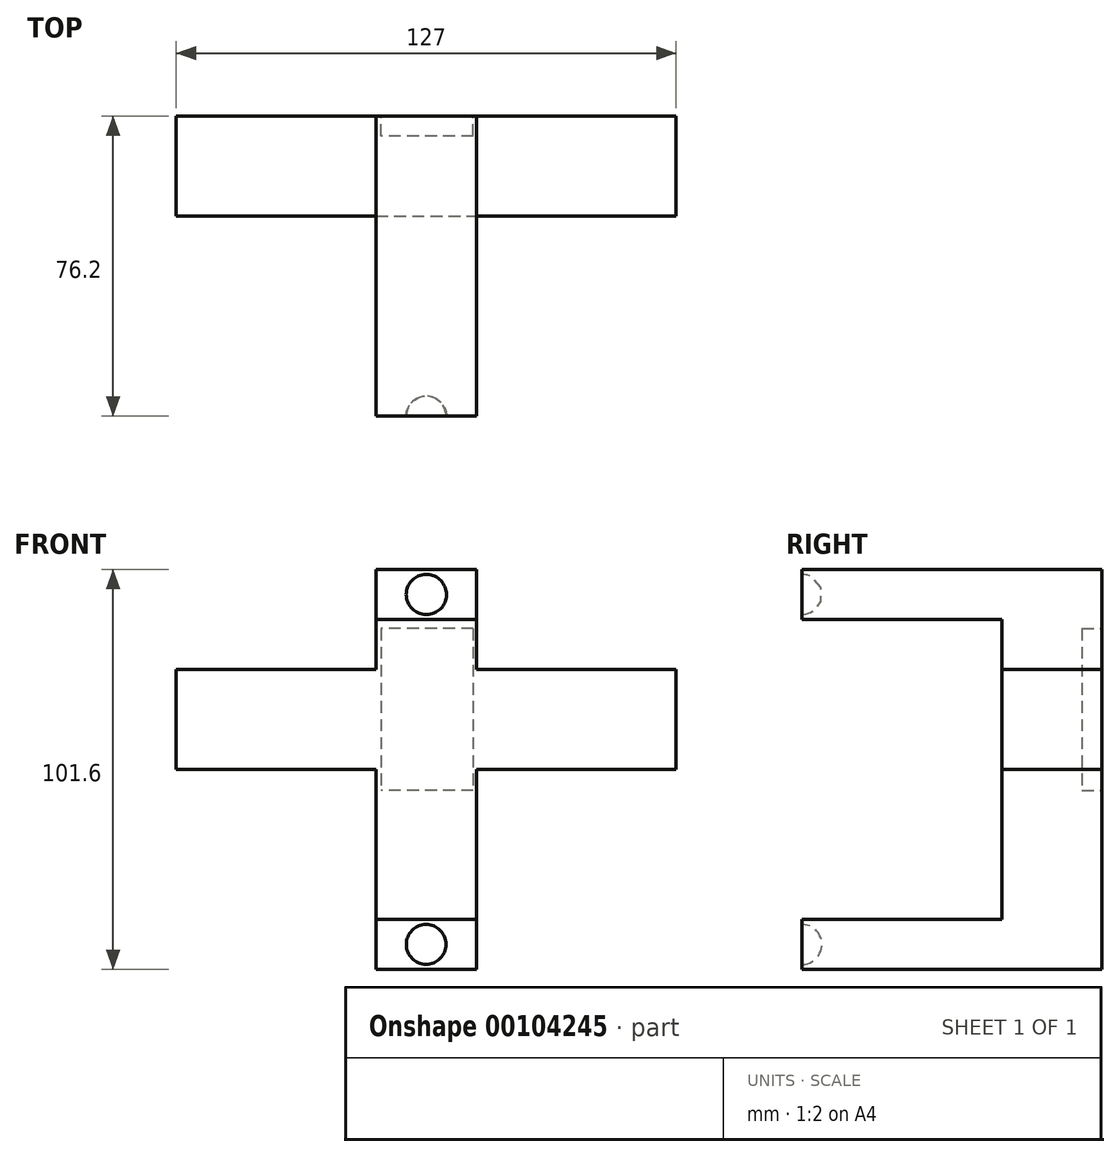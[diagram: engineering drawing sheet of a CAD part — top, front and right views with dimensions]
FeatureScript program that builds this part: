
annotation { "Feature Type Name" : "Feature", "Feature Type Description" : "" }
export const myFeature = defineFeature(function(context is Context, id is Id, definition is map)
    precondition{}
    {
        {
            var Q0;
            Q0=qCreatedBy(makeId("Front.planeOp"),FACE);
            var sketch = newSketch(context, id + "F0", { "sketchPlane" : qUnion([Q0])});
            skLineSegment(sketch, "E0.bottom", {"start": v(-67.58, 4.59) * mm, "end": v(59.42, 4.59) * mm});
            skLineSegment(sketch, "E0.top", {"start": v(-67.58, -20.81) * mm, "end": v(59.42, -20.81) * mm});
            skLineSegment(sketch, "E0.left", {"start": v(-67.58, 4.59) * mm, "end": v(-67.58, -20.81) * mm});
            skLineSegment(sketch, "E0.right", {"start": v(59.42, 4.59) * mm, "end": v(59.42, -20.81) * mm});
            skSolve(sketch);
        }
        {
            var Q0;
            Q0=makeQuery(id+"F0.imprint","IMPRINT",FACE,{"disambiguationData":[TD([[makeQuery(id+"F0.imprint","IMPRINT",EDGE,{"derivedFrom":sQuery(id+"F0.wireOp",EDGE,"E0.bottom")}),-1.0]])]});
            extrude(context, id + "F1", {"entities" : qUnion([Q0]), "depth" : 25.4 * mm});
        }
        {
            var Q0;
            Q0=makeQuery(id+"F1.opExtrude","SWEPT_FACE",FACE,{"disambiguationData":[OSD([sQuery(id+"F0.wireOp",EDGE,"E0.top")])]});
            var sketch = newSketch(context, id + "F2", { "sketchPlane" : qUnion([Q0])});
            skLineSegment(sketch, "E1", {"start": v(-16.78, 25.4) * mm, "end": v(-16.78, 0) * mm});
            skLineSegment(sketch, "E2", {"start": v(8.69, 25.4) * mm, "end": v(8.69, 0) * mm});
            skSolve(sketch);
        }
        {
            var Q0;
            {var subQ0=sQuery(id+"F2.wireOp",EDGE,"E1");Q0=makeQuery(id+"F2.imprint","IMPRINT",FACE,{"disambiguationData":[TD([[makeQuery(id+"F2.imprint","IMPRINT",EDGE,{"derivedFrom":subQ0}),1.0]])]});}
            extrude(context, id + "F3", {"entities" : qUnion([Q0]), "operationType" : NewBodyOperationType.ADD, "endBound" : BoundingType.SYMMETRIC, "depth" : 101.6 * mm});
        }
        {
            var Q0;
            {var subQ0=sQuery(id+"F0.wireOp",EDGE,"E0.top");var subQ1=makeQuery(id+"F1.opExtrude","CAP_EDGE",EDGE,{"disambiguationData":[OSD([subQ0])],"isStart":false});Q0=makeQuery(id+"F3.boolean.opBoolean","MERGE",FACE,{"derivedFrom":[makeQuery(id+"F1.opExtrude","CAP_FACE",FACE,{"disambiguationData":[OSD([sQuery(id+"F0.wireOp",EDGE,"E0.bottom"),subQ0,sQuery(id+"F0.wireOp",EDGE,"E0.left"),sQuery(id+"F0.wireOp",EDGE,"E0.right")])],"isStart":false}),makeQuery(id+"F3.opExtrude","SWEPT_FACE",FACE,{"disambiguationData":[OSD([subQ0]),TDD([makeQuery(id+"F2.imprint","IMPRINT",EDGE,{"disambiguationData":[TD([[makeQuery(id+"F2.imprint","INTERSECT",VERTEX,{"derivedFrom":[subQ1,sQuery(id+"F2.wireOp",EDGE,"E1")]}),-1.0]])],"derivedFrom":subQ1})])]})]});}
            var sketch = newSketch(context, id + "F4", { "sketchPlane" : qUnion([Q0])});
            skLineSegment(sketch, "E3", {"start": v(-16.78, 17.29) * mm, "end": v(8.69, 17.29) * mm});
            skLineSegment(sketch, "E4", {"start": v(-16.78, -58.91) * mm, "end": v(8.69, -58.91) * mm});
            skSolve(sketch);
        }
        {
            var Q0;
            {var subQ0=sQuery(id+"F4.wireOp",EDGE,"E3");Q0=makeQuery(id+"F4.imprint","IMPRINT",FACE,{"disambiguationData":[TD([[makeQuery(id+"F4.imprint","IMPRINT",EDGE,{"derivedFrom":subQ0}),1.0]])]});}
            var Q1;
            {var subQ0=sQuery(id+"F4.wireOp",EDGE,"E4");Q1=makeQuery(id+"F4.imprint","IMPRINT",FACE,{"disambiguationData":[TD([[makeQuery(id+"F4.imprint","IMPRINT",EDGE,{"derivedFrom":subQ0}),-1.0]])]});}
            extrude(context, id + "F5", {"entities" : qUnion([Q0, Q1]), "operationType" : NewBodyOperationType.ADD, "depth" : 50.8 * mm});
        }
        {
            var Q0;
            Q0=makeQuery(id+"F5.opExtrude","CAP_FACE",FACE,{"disambiguationData":[OSD([sQuery(id+"F0.wireOp",EDGE,"E0.top"),sQuery(id+"F2.wireOp",EDGE,"E1"),sQuery(id+"F2.wireOp",EDGE,"E2"),sQuery(id+"F4.wireOp",EDGE,"E3")])],"isStart":false});
            var sketch = newSketch(context, id + "F6", { "sketchPlane" : qUnion([Q0])});
            skLineSegment(sketch, "E5", {"start": v(-16.78, 28.72) * mm, "end": v(8.69, 28.72) * mm});
            skLineSegment(sketch, "E6", {"start": v(8.69, 28.72) * mm, "end": v(8.69, 29.99) * mm});
            skLineSegment(sketch, "E7", {"start": v(-16.78, 18.56) * mm, "end": v(8.69, 18.56) * mm});
            skLineSegment(sketch, "E8", {"start": v(8.69, 18.56) * mm, "end": v(8.69, 17.29) * mm});
            skLineSegment(sketch, "E9", {"start": v(-4.05, 18.56) * mm, "end": v(-4, 28.72) * mm});
            skLineSegment(sketch, "E10", {"start": v(-9.16, 28.72) * mm, "end": v(-9.16, 18.56) * mm});
            skArc(sketch, "E11", {"start": v(-4, 28.72) * mm, "mid": v(-9.14, 23.66) * mm, "end": v(-4.05, 18.56) * mm});
            skSolve(sketch);
        }
        {
            var Q0;
            {var subQ1=sQuery(id+"F6.wireOp",EDGE,"E9");Q0=makeQuery(id+"F6.imprint","IMPRINT",FACE,{"disambiguationData":[TD([[makeQuery(id+"F6.imprint","IMPRINT",EDGE,{"derivedFrom":subQ1}),1.0]])]});}
            var Q1;
            Q1=sQuery(id+"F6.wireOp",EDGE,"E9");
            revolve(context, id + "F7", {"operationType" : NewBodyOperationType.REMOVE, "entities" : qUnion([Q0]), "axis" : qUnion([Q1]), "revolveType" : RevolveType.FULL, "oppositeDirection" : true});
        }
        {
            var Q0;
            Q0=makeQuery(id+"F5.opExtrude","CAP_FACE",FACE,{"disambiguationData":[OSD([sQuery(id+"F0.wireOp",EDGE,"E0.top"),sQuery(id+"F2.wireOp",EDGE,"E1"),sQuery(id+"F2.wireOp",EDGE,"E2"),sQuery(id+"F4.wireOp",EDGE,"E4")])],"isStart":false});
            var sketch = newSketch(context, id + "F8", { "sketchPlane" : qUnion([Q0])});
            skLineSegment(sketch, "E12", {"start": v(8.69, -60.18) * mm, "end": v(8.69, -58.91) * mm});
            skLineSegment(sketch, "E13", {"start": v(-4.08, -60.18) * mm, "end": v(-4.08, -70.34) * mm});
            skPoint(sketch, "E13.startSnap0", {"position": v(-4.05, -60.18) * mm});
            skLineSegment(sketch, "E14", {"start": v(-9.16, -60.18) * mm, "end": v(-9.16, -70.34) * mm});
            skArc(sketch, "E15", {"start": v(-4.05, -60.18) * mm, "mid": v(-9.13, -65.24) * mm, "end": v(-4.08, -70.34) * mm});
            skSolve(sketch);
        }
        {
            var Q0;
            {var subQ0=sQuery(id+"F8.wireOp",EDGE,"E15");var subQ1=sQuery(id+"F8.wireOp",EDGE,"E13");var subQ2=makeQuery(id+"F8.imprint","INTERSECT",VERTEX,{"disambiguationData":[OD(0.0)],"derivedFrom":[subQ1,subQ0]});Q0=makeQuery(id+"F8.imprint","IMPRINT",FACE,{"disambiguationData":[TD([[makeQuery(id+"F8.imprint","IMPRINT",EDGE,{"disambiguationData":[TD([[subQ2,1.0]])],"derivedFrom":subQ1}),-1.0]])]});}
            var Q1;
            Q1=sQuery(id+"F8.wireOp",EDGE,"E13");
            revolve(context, id + "F9", {"operationType" : NewBodyOperationType.REMOVE, "entities" : qUnion([Q0]), "axis" : qUnion([Q1]), "revolveType" : RevolveType.FULL, "oppositeDirection" : true});
        }
        {
            var Q0;
            {var subQ0=sQuery(id+"F0.wireOp",EDGE,"E0.top");var subQ1=makeQuery(id+"F1.opExtrude","CAP_EDGE",EDGE,{"disambiguationData":[OSD([subQ0])],"isStart":true});Q0=makeQuery(id+"F3.boolean.opBoolean","MERGE",FACE,{"derivedFrom":[makeQuery(id+"F1.opExtrude","CAP_FACE",FACE,{"disambiguationData":[OSD([sQuery(id+"F0.wireOp",EDGE,"E0.bottom"),subQ0,sQuery(id+"F0.wireOp",EDGE,"E0.left"),sQuery(id+"F0.wireOp",EDGE,"E0.right")])],"isStart":true}),makeQuery(id+"F3.opExtrude","SWEPT_FACE",FACE,{"disambiguationData":[OSD([subQ0]),TDD([makeQuery(id+"F2.imprint","IMPRINT",EDGE,{"disambiguationData":[TD([[makeQuery(id+"F2.imprint","INTERSECT",VERTEX,{"derivedFrom":[subQ1,sQuery(id+"F2.wireOp",EDGE,"E1")]}),-1.0]])],"derivedFrom":subQ1})])]})]});}
            var sketch = newSketch(context, id + "F10", { "sketchPlane" : qUnion([Q0])});
            skLineSegment(sketch, "E16.bottom", {"start": v(-7.85, 14.96) * mm, "end": v(15.51, 14.96) * mm});
            skLineSegment(sketch, "E16.top", {"start": v(-7.85, -26.19) * mm, "end": v(15.51, -26.19) * mm});
            skLineSegment(sketch, "E16.left", {"start": v(-7.85, 14.96) * mm, "end": v(-7.85, -26.19) * mm});
            skLineSegment(sketch, "E16.right", {"start": v(15.51, 14.96) * mm, "end": v(15.51, -26.19) * mm});
            skSolve(sketch);
        }
        {
            var Q0;
            Q0=makeQuery(id+"F10.imprint","IMPRINT",FACE,{"disambiguationData":[TD([[makeQuery(id+"F10.imprint","IMPRINT",EDGE,{"derivedFrom":sQuery(id+"F10.wireOp",EDGE,"E16.bottom")}),-1.0]])]});
            extrude(context, id + "F11", {"entities" : qUnion([Q0]), "operationType" : NewBodyOperationType.REMOVE, "oppositeDirection" : true, "depth" : 5.08 * mm});
        }
    });
